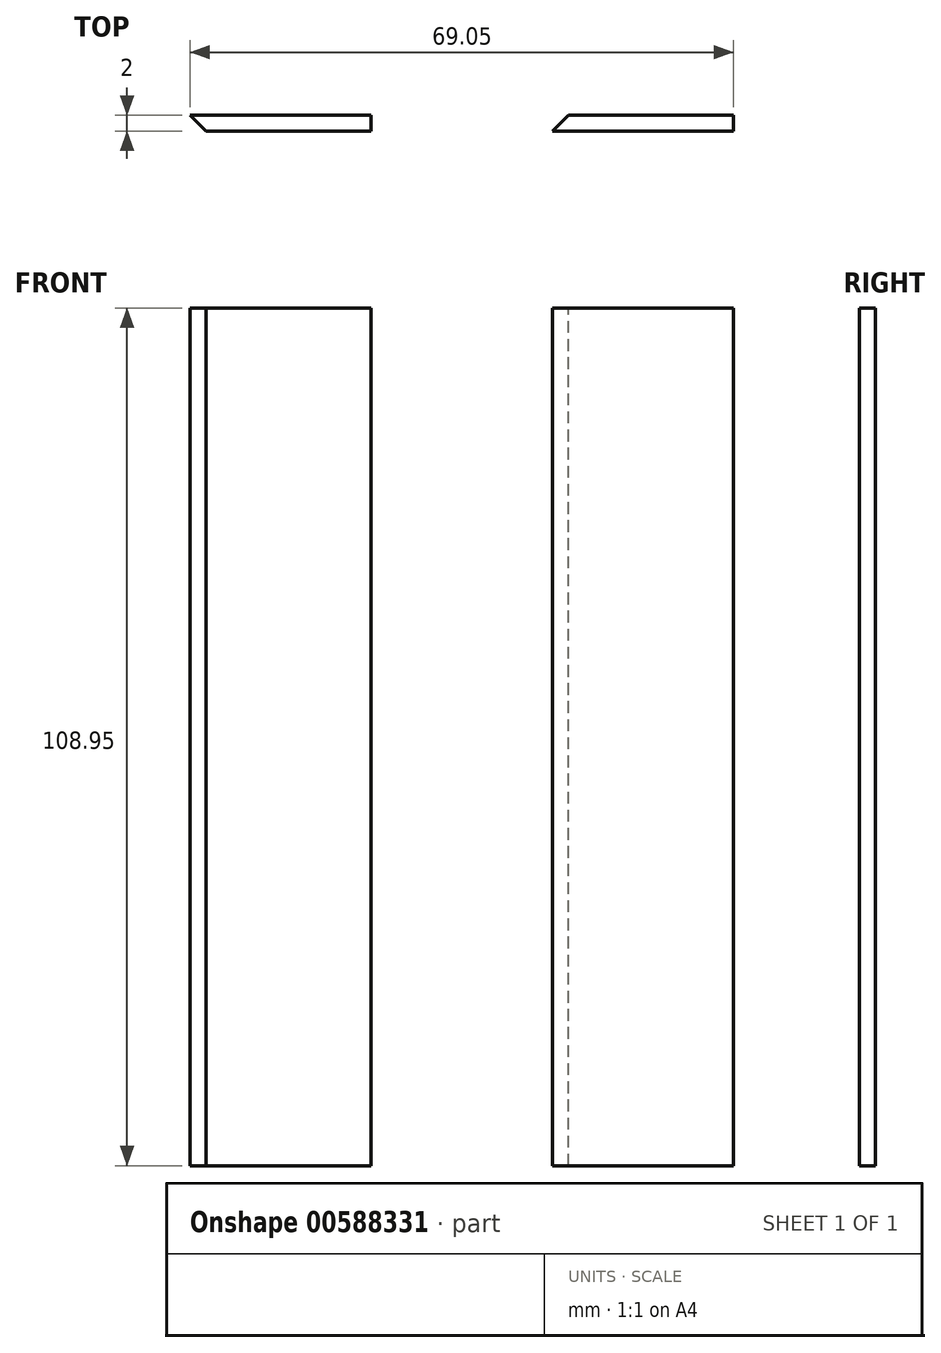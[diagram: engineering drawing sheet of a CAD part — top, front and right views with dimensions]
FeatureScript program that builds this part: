
annotation { "Feature Type Name" : "Feature", "Feature Type Description" : "" }
export const myFeature = defineFeature(function(context is Context, id is Id, definition is map)
    precondition{}
    {
        {
            var Q0;
            Q0=qCreatedBy(makeId("Front.planeOp"),FACE);
            var sketch = newSketch(context, id + "F0", { "sketchPlane" : qUnion([Q0])});
            skLineSegment(sketch, "E0", {"start": v(-75.93, -44.32) * mm, "end": v(-77.93, -44.32) * mm});
            skLineSegment(sketch, "E1", {"start": v(-77.93, -44.32) * mm, "end": v(-98.93, -44.32) * mm});
            skLineSegment(sketch, "E2", {"start": v(-98.93, -44.32) * mm, "end": v(-98.93, 64.63) * mm});
            skPoint(sketch, "E3.endSnap0", {"position": v(-98.93, 10.16) * mm});
            skPoint(sketch, "E3.end.orphan", {"position": v(-122.21, 10.16) * mm});
            skLineSegment(sketch, "E4", {"start": v(-75.93, -44.32) * mm, "end": v(-75.93, 64.63) * mm});
            skLineSegment(sketch, "E5", {"start": v(-75.93, 64.63) * mm, "end": v(-98.93, 64.63) * mm});
            skLineSegment(sketch, "E6", {"start": v(-31.88, -44.32) * mm, "end": v(-52.88, -44.32) * mm});
            skLineSegment(sketch, "E7", {"start": v(-52.88, -44.32) * mm, "end": v(-52.88, 64.63) * mm});
            skLineSegment(sketch, "E8", {"start": v(-29.88, -44.32) * mm, "end": v(-29.88, 64.63) * mm});
            skLineSegment(sketch, "E9", {"start": v(-29.88, 64.63) * mm, "end": v(-52.88, 64.63) * mm});
            skLineSegment(sketch, "E10", {"start": v(-31.88, -44.32) * mm, "end": v(-29.88, -44.32) * mm});
            skSolve(sketch);
        }
        {
            var Q0;
            Q0=makeQuery(id+"F0.imprint","IMPRINT",FACE,{"disambiguationData":[TD([[makeQuery(id+"F0.imprint","IMPRINT",EDGE,{"derivedFrom":sQuery(id+"F0.wireOp",EDGE,"E0")}),-1.0]])]});
            var Q1;
            Q1=makeQuery(id+"F0.imprint","IMPRINT",FACE,{"disambiguationData":[TD([[makeQuery(id+"F0.imprint","IMPRINT",EDGE,{"derivedFrom":sQuery(id+"F0.wireOp",EDGE,"E6")}),-1.0]])]});
            extrude(context, id + "F1", {"entities" : qUnion([Q0, Q1]), "depth" : 2 * mm, "offsetDistance" : 25 * mm});
        }
        {
            var Q0;
            Q0=makeQuery(id+"F1.opExtrude","SWEPT_FACE",FACE,{"disambiguationData":[OSD([sQuery(id+"F0.wireOp",EDGE,"E5")])]});
            var sketch = newSketch(context, id + "F2", { "sketchPlane" : qUnion([Q0])});
            skLineSegment(sketch, "E11", {"start": v(-98.93, -2) * mm, "end": v(-96.93, -2) * mm});
            skLineSegment(sketch, "E12", {"start": v(-98.93, 0) * mm, "end": v(-96.93, -2) * mm});
            skSolve(sketch);
        }
        {
            var Q0;
            Q0=makeQuery(id+"F2.imprint","IMPRINT",FACE,{"disambiguationData":[TD([[makeQuery(id+"F2.imprint","IMPRINT",EDGE,{"derivedFrom":sQuery(id+"F2.wireOp",EDGE,"E11")}),-1.0]])]});
            extrude(context, id + "F3", {"entities" : qUnion([Q0]), "operationType" : NewBodyOperationType.REMOVE, "oppositeDirection" : true, "depth" : 250 * mm, "offsetDistance" : 25 * mm});
        }
        {
            var Q0;
            Q0=makeQuery(id+"F1.opExtrude","SWEPT_FACE",FACE,{"disambiguationData":[OSD([sQuery(id+"F0.wireOp",EDGE,"E9")])]});
            var sketch = newSketch(context, id + "F4", { "sketchPlane" : qUnion([Q0])});
            skLineSegment(sketch, "E13", {"start": v(-29.88, 0) * mm, "end": v(-31.88, 0) * mm});
            skLineSegment(sketch, "E14", {"start": v(-31.88, 0) * mm, "end": v(-29.88, -2) * mm});
            skLineSegment(sketch, "E15", {"start": v(-52.88, -2) * mm, "end": v(-52.88, 0) * mm});
            skLineSegment(sketch, "E16", {"start": v(-52.88, 0) * mm, "end": v(-50.88, 0) * mm});
            skLineSegment(sketch, "E17", {"start": v(-50.88, 0) * mm, "end": v(-52.88, -2) * mm});
            skSolve(sketch);
        }
        {
            var Q0;
            Q0=makeQuery(id+"F4.imprint","IMPRINT",FACE,{"disambiguationData":[TD([[makeQuery(id+"F4.imprint","IMPRINT",EDGE,{"derivedFrom":sQuery(id+"F4.wireOp",EDGE,"E15")}),-1.0]])]});
            extrude(context, id + "F5", {"entities" : qUnion([Q0]), "operationType" : NewBodyOperationType.REMOVE, "oppositeDirection" : true, "depth" : 250 * mm, "offsetDistance" : 25 * mm});
        }
    });
